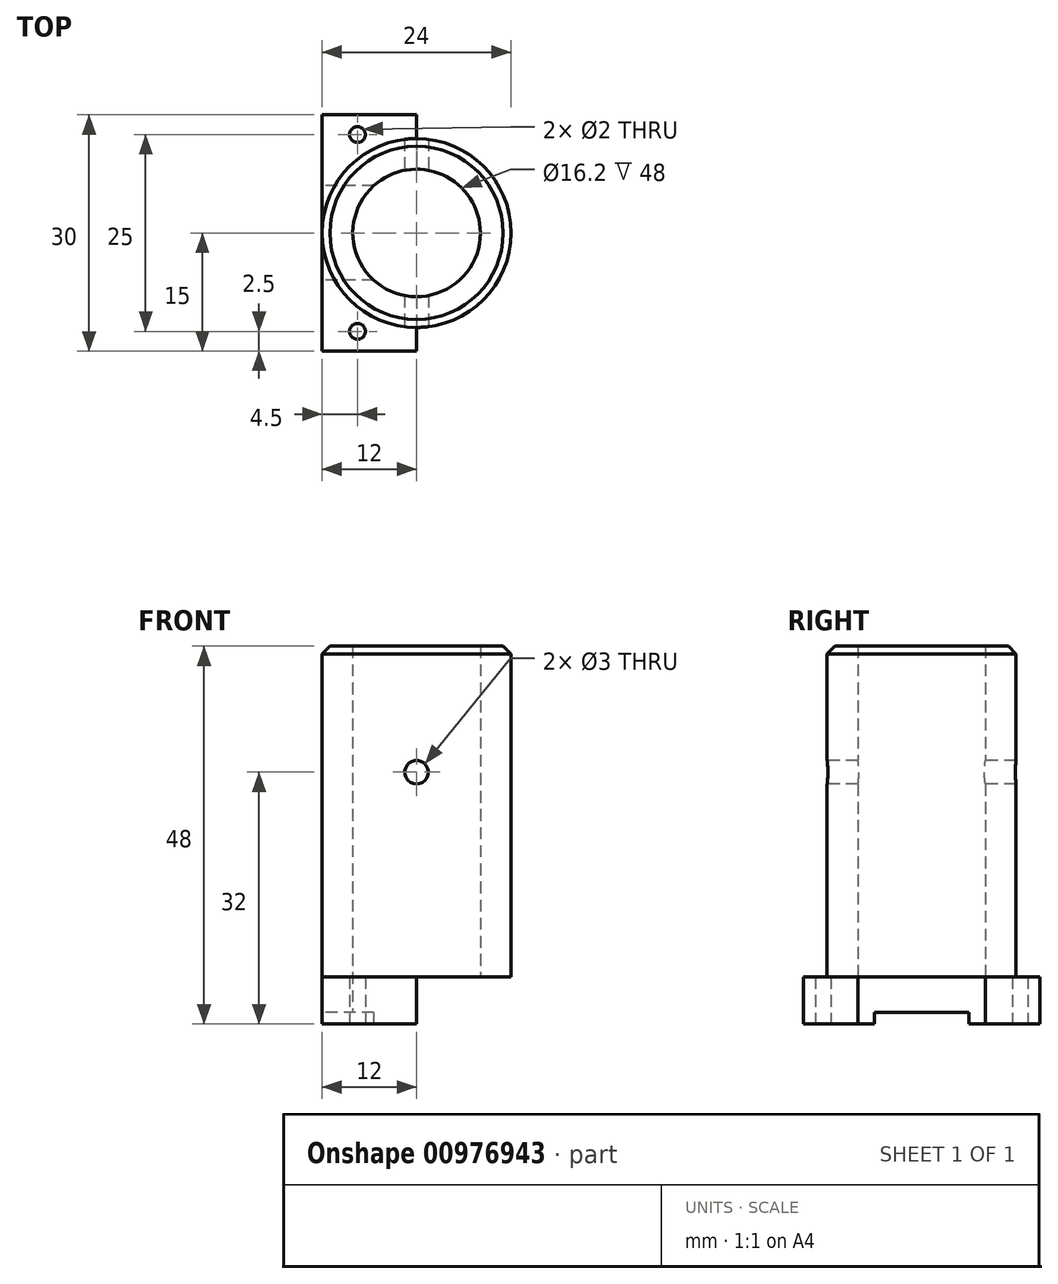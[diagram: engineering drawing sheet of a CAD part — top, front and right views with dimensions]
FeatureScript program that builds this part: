
annotation { "Feature Type Name" : "Feature", "Feature Type Description" : "" }
export const myFeature = defineFeature(function(context is Context, id is Id, definition is map)
    precondition{}
    {
        {
            var Q0;
            Q0=qCreatedBy(makeId("Top.planeOp"),FACE);
            var sketch = newSketch(context, id + "F0", { "sketchPlane" : qUnion([Q0])});
            skLineSegment(sketch, "E0.bottom", {"start": v(-6, 15) * mm, "end": v(6, 15) * mm});
            skLineSegment(sketch, "E0.top", {"start": v(-6, -15) * mm, "end": v(6, -15) * mm});
            skLineSegment(sketch, "E0.left", {"start": v(-6, 15) * mm, "end": v(-6, -15) * mm});
            skLineSegment(sketch, "E0.right", {"start": v(6, 15) * mm, "end": v(6, -15) * mm});
            skCircle(sketch, "E1", {"center": v(-1.5, 12.5) * mm, "radius": 1 * mm});
            skCircle(sketch, "E2", {"center": v(-1.5, -12.5) * mm, "radius": 1 * mm});
            skSolve(sketch);
        }
        {
            var Q0;
            Q0 = qSketchRegion(id + "F0", true);
            extrude(context, id + "F1", {"entities" : qUnion([Q0]), "depth" : 6 * mm, "offsetDistance" : 25 * mm});
        }
        {
            var Q0;
            Q0=makeQuery(id+"F1.opExtrude","CAP_FACE",FACE,{"disambiguationData":[OSD([sQuery(id+"F0.wireOp",EDGE,"E0.bottom"),sQuery(id+"F0.wireOp",EDGE,"E0.top"),sQuery(id+"F0.wireOp",EDGE,"E0.left"),sQuery(id+"F0.wireOp",EDGE,"E0.right"),sQuery(id+"F0.wireOp",EDGE,"E1"),sQuery(id+"F0.wireOp",EDGE,"E2")])],"isStart":false});
            var sketch = newSketch(context, id + "F2", { "sketchPlane" : qUnion([Q0])});
            skCircle(sketch, "E3", {"center": v(6, 0) * mm, "radius": 12 * mm});
            skCircle(sketch, "E4", {"center": v(6, 0) * mm, "radius": 8.1 * mm});
            skSolve(sketch);
        }
        {
            var Q0;
            Q0 = qSketchRegion(id + "F2", true);
            extrude(context, id + "F3", {"entities" : qUnion([Q0]), "operationType" : NewBodyOperationType.ADD, "depth" : 42 * mm, "offsetDistance" : 25 * mm});
        }
        {
            var Q0;
            {var subQ0=sQuery(id+"F0.wireOp",EDGE,"E0.right");var subQ1=sQuery(id+"F2.wireOp",EDGE,"E4");Q0=makeQuery(id+"F3.boolean.opBoolean","SPLIT",FACE,{"disambiguationData":[TD([makeQuery(id+"F3.opExtrude","SWEPT_FACE",FACE,{"disambiguationData":[OSD([subQ1])]})])],"derivedFrom":makeQuery(id+"F1.opExtrude","CAP_FACE",FACE,{"disambiguationData":[OSD([sQuery(id+"F0.wireOp",EDGE,"E0.bottom"),sQuery(id+"F0.wireOp",EDGE,"E0.top"),sQuery(id+"F0.wireOp",EDGE,"E0.left"),subQ0,sQuery(id+"F0.wireOp",EDGE,"E1"),sQuery(id+"F0.wireOp",EDGE,"E2")])],"isStart":false})});}
            extrude(context, id + "F4", {"entities" : qUnion([Q0]), "operationType" : NewBodyOperationType.REMOVE, "endBound" : BoundingType.THROUGH_ALL, "oppositeDirection" : true, "depth" : 25 * mm, "offsetDistance" : 25 * mm});
        }
        {
            var Q0;
            Q0=makeQuery(id+"F1.opExtrude","SWEPT_FACE",FACE,{"disambiguationData":[OSD([sQuery(id+"F0.wireOp",EDGE,"E0.left")])]});
            var sketch = newSketch(context, id + "F5", { "sketchPlane" : qUnion([Q0])});
            skLineSegment(sketch, "E5.bottom", {"start": v(-6, 0) * mm, "end": v(6, 0) * mm});
            skLineSegment(sketch, "E5.top", {"start": v(-6, 1.5) * mm, "end": v(6, 1.5) * mm});
            skLineSegment(sketch, "E5.left", {"start": v(-6, 0) * mm, "end": v(-6, 1.5) * mm});
            skLineSegment(sketch, "E5.right", {"start": v(6, 0) * mm, "end": v(6, 1.5) * mm});
            skSolve(sketch);
        }
        {
            var Q0;
            Q0 = qSketchRegion(id + "F5", true);
            extrude(context, id + "F6", {"entities" : qUnion([Q0]), "operationType" : NewBodyOperationType.REMOVE, "endBound" : BoundingType.THROUGH_ALL, "oppositeDirection" : true, "depth" : 25 * mm, "offsetDistance" : 25 * mm});
        }
        {
            var Q0;
            Q0=qCreatedBy(makeId("Front.planeOp"),FACE);
            var sketch = newSketch(context, id + "F7", { "sketchPlane" : qUnion([Q0])});
            skCircle(sketch, "E6", {"center": v(6, 32) * mm, "radius": 1.5 * mm});
            skSolve(sketch);
        }
        {
            var Q0;
            Q0 = qSketchRegion(id + "F7", true);
            extrude(context, id + "F8", {"entities" : qUnion([Q0]), "operationType" : NewBodyOperationType.REMOVE, "endBound" : BoundingType.THROUGH_ALL, "oppositeDirection" : true, "depth" : 25 * mm, "offsetDistance" : 25 * mm, "hasSecondDirection" : true, "secondDirectionBound" : BoundingType.THROUGH_ALL, "secondDirectionOppositeDirection" : false, "secondDirectionDepth" : 25 * mm});
        }
        {
            var Q0;
            Q0=makeQuery(id+"F3.opExtrude","CAP_EDGE",EDGE,{"disambiguationData":[OSD([sQuery(id+"F2.wireOp",EDGE,"E3")])],"isStart":false});
            chamfer(context, id + "F9", {"entities" : qUnion([Q0]), "width" : 1 * mm, "tangentPropagation" : true});
        }
    });
